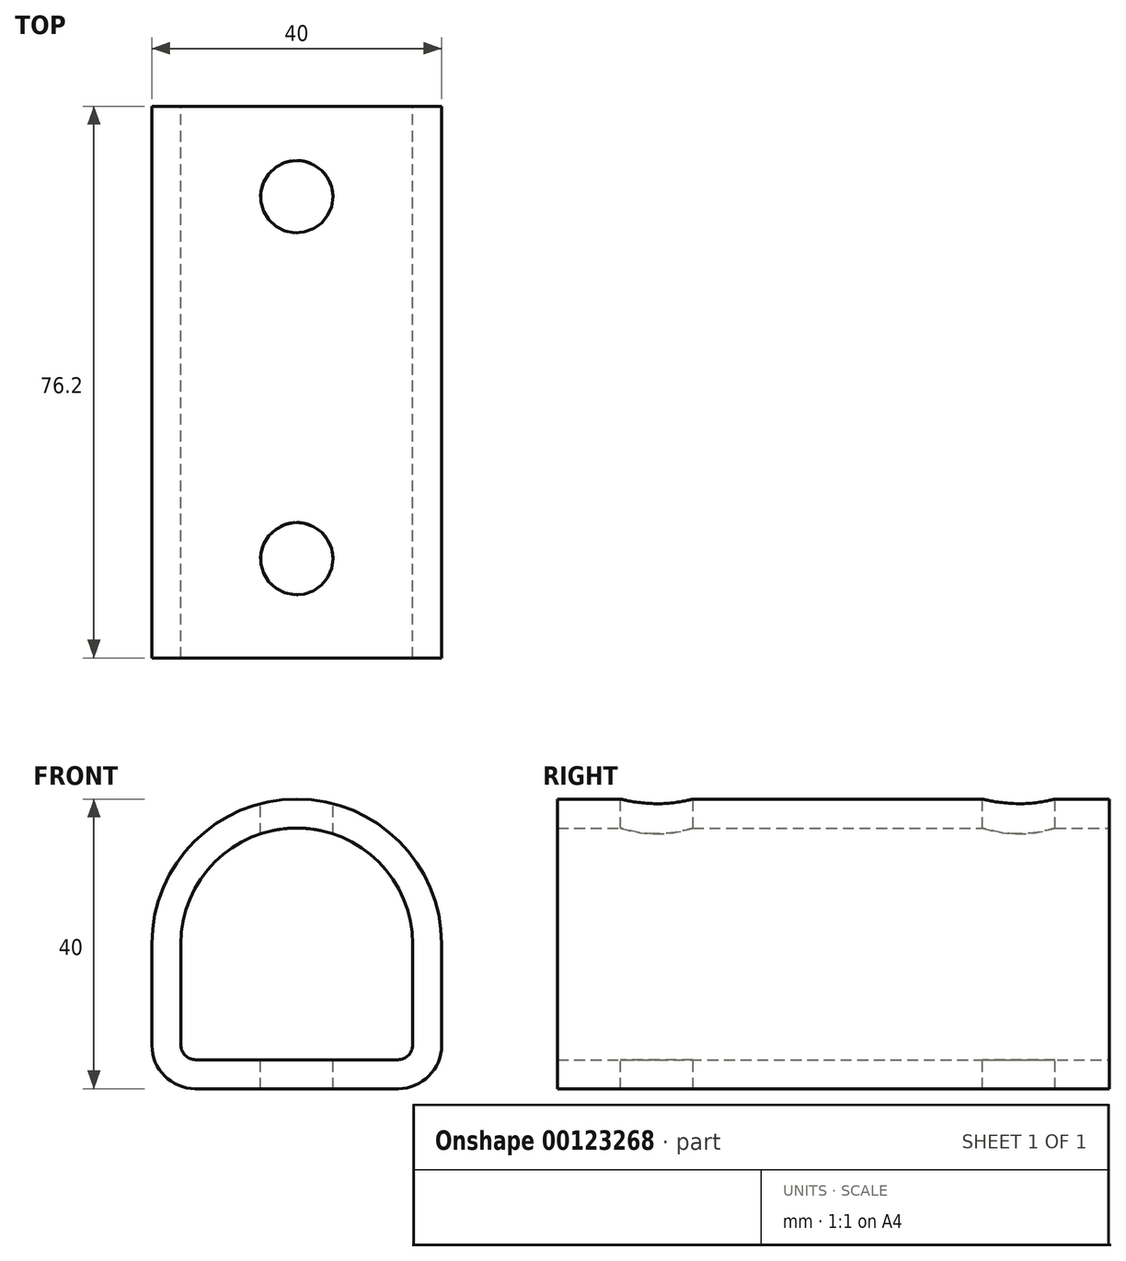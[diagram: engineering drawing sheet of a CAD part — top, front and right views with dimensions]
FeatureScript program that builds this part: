
annotation { "Feature Type Name" : "Feature", "Feature Type Description" : "" }
export const myFeature = defineFeature(function(context is Context, id is Id, definition is map)
    precondition{}
    {
        {
            var Q0;
            Q0=qCreatedBy(makeId("Front.planeOp"),FACE);
            var sketch = newSketch(context, id + "F0", { "sketchPlane" : qUnion([Q0])});
            skLineSegment(sketch, "E0", {"start": v(-20, 0) * mm, "end": v(-20, -14) * mm});
            skLineSegment(sketch, "E1", {"start": v(-14, -20) * mm, "end": v(14, -20) * mm});
            skLineSegment(sketch, "E2", {"start": v(20, -14) * mm, "end": v(20, 0) * mm});
            skArc(sketch, "E3", {"start": v(-20, 0) * mm, "mid": v(0, 20) * mm, "end": v(20, 0) * mm});
            skPoint(sketch, "E4.visualSharp", {"position": v(-20, -20) * mm});
            skArc(sketch, "E4.filletArc", {"start": v(-20, -14) * mm, "mid": v(-18.24, -18.24) * mm, "end": v(-14, -20) * mm});
            skPoint(sketch, "E5.visualSharp", {"position": v(20, -20) * mm});
            skArc(sketch, "E5.filletArc", {"start": v(14, -20) * mm, "mid": v(18.24, -18.24) * mm, "end": v(20, -14) * mm});
            skArc(sketch, "E6.0", {"start": v(-16, 0) * mm, "mid": v(0, 16) * mm, "end": v(16, 0) * mm});
            skLineSegment(sketch, "E6.1", {"start": v(-16, 0) * mm, "end": v(-16, -13.97) * mm});
            skLineSegment(sketch, "E6.2", {"start": v(-13.97, -16) * mm, "end": v(13.97, -16) * mm});
            skLineSegment(sketch, "E6.3", {"start": v(16, -13.97) * mm, "end": v(16, 0) * mm});
            skPoint(sketch, "E7.visualSharp", {"position": v(-16, -16) * mm});
            skArc(sketch, "E7.filletArc", {"start": v(-16, -13.97) * mm, "mid": v(-15.4, -15.4) * mm, "end": v(-13.97, -16) * mm});
            skPoint(sketch, "E8.visualSharp", {"position": v(16, -16) * mm});
            skArc(sketch, "E8.filletArc", {"start": v(13.97, -16) * mm, "mid": v(15.4, -15.4) * mm, "end": v(16, -13.97) * mm});
            skSolve(sketch);
        }
        {
            var Q0;
            Q0=makeQuery(id+"F0.imprint","IMPRINT",FACE,{"disambiguationData":[TD([[makeQuery(id+"F0.imprint","IMPRINT",EDGE,{"derivedFrom":sQuery(id+"F0.wireOp",EDGE,"E0")}),1.0]])]});
            extrude(context, id + "F1", {"entities" : qUnion([Q0]), "depth" : 76.2 * mm});
        }
        {
            var Q0;
            Q0=qCreatedBy(makeId("Top.planeOp"),FACE);
            var sketch = newSketch(context, id + "F2", { "sketchPlane" : qUnion([Q0])});
            skCircle(sketch, "E9", {"center": v(0, -62.5) * mm, "radius": 5 * mm});
            skCircle(sketch, "E10", {"center": v(0, -12.5) * mm, "radius": 5 * mm});
            skSolve(sketch);
        }
        {
            var Q0;
            Q0 = qSketchRegion(id + "F2", true);
            extrude(context, id + "F3", {"entities" : qUnion([Q0]), "operationType" : NewBodyOperationType.REMOVE, "endBound" : BoundingType.THROUGH_ALL, "oppositeDirection" : true, "depth" : 25.4 * mm, "hasSecondDirection" : true, "secondDirectionOppositeDirection" : false, "secondDirectionDepth" : 25.4 * mm});
        }
    });
